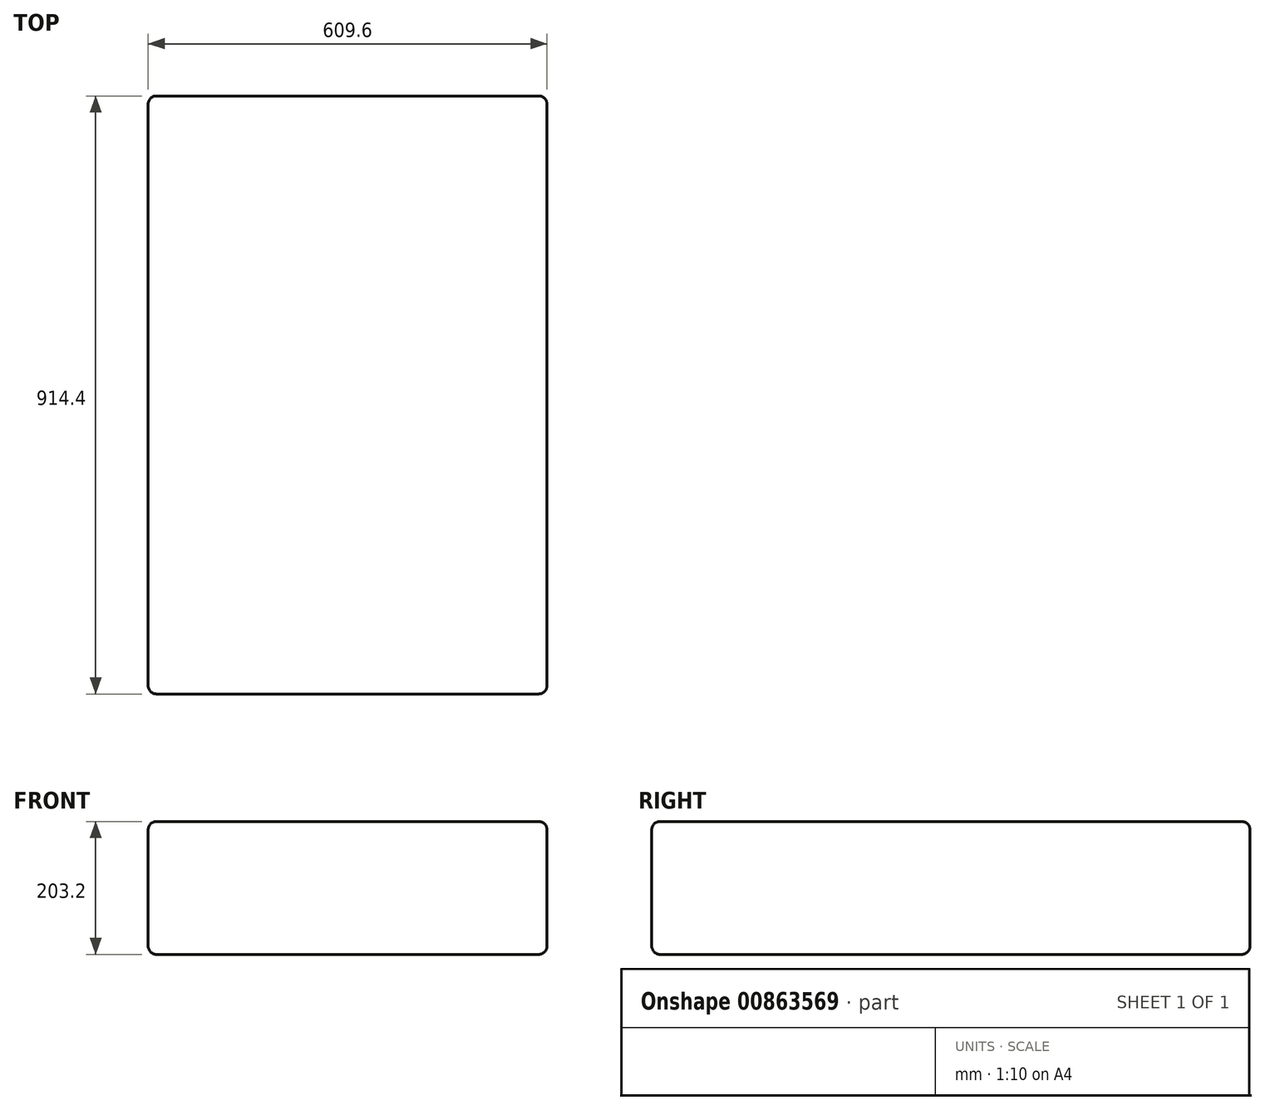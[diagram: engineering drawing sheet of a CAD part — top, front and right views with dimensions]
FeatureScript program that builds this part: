
annotation { "Feature Type Name" : "Feature", "Feature Type Description" : "" }
export const myFeature = defineFeature(function(context is Context, id is Id, definition is map)
    precondition{}
    {
        {
            var Q0;
            Q0=qCreatedBy(makeId("Top.planeOp"),FACE);
            var sketch = newSketch(context, id + "F0", { "sketchPlane" : qUnion([Q0])});
            skLineSegment(sketch, "E0.bottom", {"start": v(-380.08, 514.19) * mm, "end": v(229.52, 514.19) * mm});
            skLineSegment(sketch, "E0.top", {"start": v(-380.08, -400.21) * mm, "end": v(229.52, -400.21) * mm});
            skLineSegment(sketch, "E0.left", {"start": v(-380.08, 514.19) * mm, "end": v(-380.08, -400.21) * mm});
            skLineSegment(sketch, "E0.right", {"start": v(229.52, 514.19) * mm, "end": v(229.52, -400.21) * mm});
            skSolve(sketch);
        }
        {
            var Q0;
            Q0=makeQuery(id+"F0.imprint","IMPRINT",FACE,{"disambiguationData":[TD([[makeQuery(id+"F0.imprint","IMPRINT",EDGE,{"derivedFrom":sQuery(id+"F0.wireOp",EDGE,"E0.bottom")}),-1.0]])]});
            extrude(context, id + "F1", {"entities" : qUnion([Q0]), "depth" : 203.2 * mm, "offsetDistance" : 25.4 * mm});
        }
        {
            var Q0;
            Q0=makeQuery(id+"F1.opExtrude","SWEPT_FACE",FACE,{"disambiguationData":[OSD([sQuery(id+"F0.wireOp",EDGE,"E0.bottom")])]});
            var Q1;
            Q1=makeQuery(id+"F1.opExtrude","SWEPT_EDGE",EDGE,{"disambiguationData":[OSD([sQuery(id+"F0.wireOp",EDGE,"E0.bottom"),sQuery(id+"F0.wireOp",EDGE,"E0.right")])]});
            var Q2;
            Q2=makeQuery(id+"F1.opExtrude","CAP_FACE",FACE,{"disambiguationData":[OSD([sQuery(id+"F0.wireOp",EDGE,"E0.bottom"),sQuery(id+"F0.wireOp",EDGE,"E0.top"),sQuery(id+"F0.wireOp",EDGE,"E0.left"),sQuery(id+"F0.wireOp",EDGE,"E0.right")])],"isStart":true});
            var Q3;
            Q3=makeQuery(id+"F1.opExtrude","SWEPT_EDGE",EDGE,{"disambiguationData":[OSD([sQuery(id+"F0.wireOp",EDGE,"E0.top"),sQuery(id+"F0.wireOp",EDGE,"E0.left")])]});
            var Q4;
            Q4=makeQuery(id+"F1.opExtrude","CAP_FACE",FACE,{"disambiguationData":[OSD([sQuery(id+"F0.wireOp",EDGE,"E0.bottom"),sQuery(id+"F0.wireOp",EDGE,"E0.top"),sQuery(id+"F0.wireOp",EDGE,"E0.left"),sQuery(id+"F0.wireOp",EDGE,"E0.right")])],"isStart":false});
            var Q5;
            Q5=makeQuery(id+"F1.opExtrude","SWEPT_EDGE",EDGE,{"disambiguationData":[OSD([sQuery(id+"F0.wireOp",EDGE,"E0.top"),sQuery(id+"F0.wireOp",EDGE,"E0.right")])]});
            var Q6;
            Q6=makeQuery(id+"F1.opExtrude","SWEPT_FACE",FACE,{"disambiguationData":[OSD([sQuery(id+"F0.wireOp",EDGE,"E0.top")])]});
            var Q7;
            Q7=makeQuery(id+"F1.opExtrude","SWEPT_FACE",FACE,{"disambiguationData":[OSD([sQuery(id+"F0.wireOp",EDGE,"E0.left")])]});
            var Q8;
            Q8=makeQuery(id+"F1.opExtrude","CAP_EDGE",EDGE,{"disambiguationData":[OSD([sQuery(id+"F0.wireOp",EDGE,"E0.bottom")])],"isStart":false});
            var Q9;
            Q9=makeQuery(id+"F1.opExtrude","SWEPT_FACE",FACE,{"disambiguationData":[OSD([sQuery(id+"F0.wireOp",EDGE,"E0.right")])]});
            var Q10;
            Q10=makeQuery(id+"F1.opExtrude","CAP_EDGE",EDGE,{"disambiguationData":[OSD([sQuery(id+"F0.wireOp",EDGE,"E0.top")])],"isStart":true});
            var Q11;
            Q11=makeQuery(id+"F1.opExtrude","CAP_EDGE",EDGE,{"disambiguationData":[OSD([sQuery(id+"F0.wireOp",EDGE,"E0.top")])],"isStart":false});
            var Q12;
            Q12=makeQuery(id+"F1.opExtrude","CAP_EDGE",EDGE,{"disambiguationData":[OSD([sQuery(id+"F0.wireOp",EDGE,"E0.left")])],"isStart":false});
            var Q13;
            Q13=makeQuery(id+"F1.opExtrude","CAP_EDGE",EDGE,{"disambiguationData":[OSD([sQuery(id+"F0.wireOp",EDGE,"E0.right")])],"isStart":true});
            var Q14;
            Q14=makeQuery(id+"F1.opExtrude","CAP_EDGE",EDGE,{"disambiguationData":[OSD([sQuery(id+"F0.wireOp",EDGE,"E0.right")])],"isStart":false});
            var Q15;
            Q15=makeQuery(id+"F1.opExtrude","SWEPT_EDGE",EDGE,{"disambiguationData":[OSD([sQuery(id+"F0.wireOp",EDGE,"E0.bottom"),sQuery(id+"F0.wireOp",EDGE,"E0.left")])]});
            var Q16;
            Q16=makeQuery(id+"F1.opExtrude","CAP_EDGE",EDGE,{"disambiguationData":[OSD([sQuery(id+"F0.wireOp",EDGE,"E0.bottom")])],"isStart":true});
            var Q17;
            Q17=makeQuery(id+"F1.opExtrude","CAP_EDGE",EDGE,{"disambiguationData":[OSD([sQuery(id+"F0.wireOp",EDGE,"E0.left")])],"isStart":true});
            fillet(context, id + "F2", {"entities" : qUnion([Q0, Q1, Q2, Q3, Q4, Q5, Q6, Q7, Q8, Q9, Q10, Q11, Q12, Q13, Q14, Q15, Q16, Q17]), "radius" : 12.7 * mm, "tangentPropagation" : true, "allowEdgeOverflow" : false});
        }
    });
